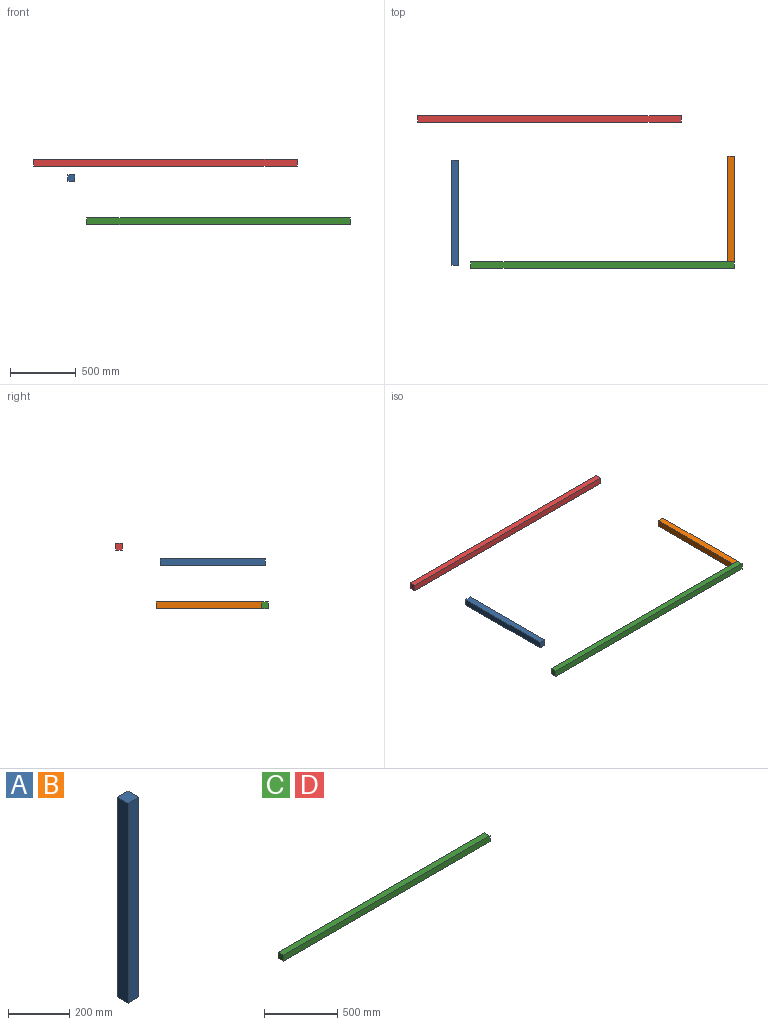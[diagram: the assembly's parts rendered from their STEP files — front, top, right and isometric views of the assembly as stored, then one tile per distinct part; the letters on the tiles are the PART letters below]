
ASSEMBLY  parts=4 mates=4
PART A: 6 faces, bbox 50x50x800 mm
  f0: plane 800x50mm, normal (-1,0,0), area 40000mm2, adj f1,f3,f4,f5
  f1: plane 800x50mm, normal (0,-1,0), area 40000mm2, adj f0,f2,f4,f5
  f2: plane 800x50mm, normal (1,0,0), area 40000mm2, adj f1,f3,f4,f5
  f3: plane 800x50mm, normal (0,1,0), area 40000mm2, adj f0,f2,f4,f5
  f4: plane 50x50mm, normal (0,0,1), area 2500mm2, adj f0,f1,f2,f3
  f5: plane 50x50mm, normal (0,0,-1), area 2500mm2, adj f0,f1,f2,f3
PART B: same geometry as A
PART C: 6 faces, bbox 2000x50x50 mm
  f0: plane 2000x50mm, normal (0,0,-1), area 100000mm2, adj f1,f3,f4,f5
  f1: plane 2000x50mm, normal (0,1,0), area 100000mm2, adj f0,f2,f4,f5
  f2: plane 2000x50mm, normal (0,0,1), area 100000mm2, adj f1,f3,f4,f5
  f3: plane 2000x50mm, normal (0,-1,0), area 100000mm2, adj f0,f2,f4,f5
  f4: plane 50x50mm, normal (1,0,0), area 2500mm2, adj f0,f1,f2,f3
  f5: plane 50x50mm, normal (-1,0,0), area 2500mm2, adj f0,f1,f2,f3
PART D: same geometry as C
PLACE A rot(axis=(-1,0,0),90deg) t=(-969.44,-896.92,430.05)mm
PLACE B rot(axis=(-1,0,0),90deg) t=(1124.76,-869.06,102.58)mm
PLACE C rot(axis=(1,0,0),180deg) t=(-825.24,-919.06,102.58)mm
PLACE D t=(-1230.22,240.13,497.08)mm
MATE planar C.f3 <-> B.f5  axis (0,1,0) through (174.76,-869.06,77.58)mm
MATE planar C.f0 <-> B.f1  axis (0,0,1) through (174.76,-894.06,102.58)mm
MATE parallel B.f2 <-> A.f2  axis (1,0,0) through (1174.76,-469.06,77.58)mm
MATE planar C.f4 <-> B.f2  axis (1,0,0) through (1174.76,-919.06,77.58)mm
